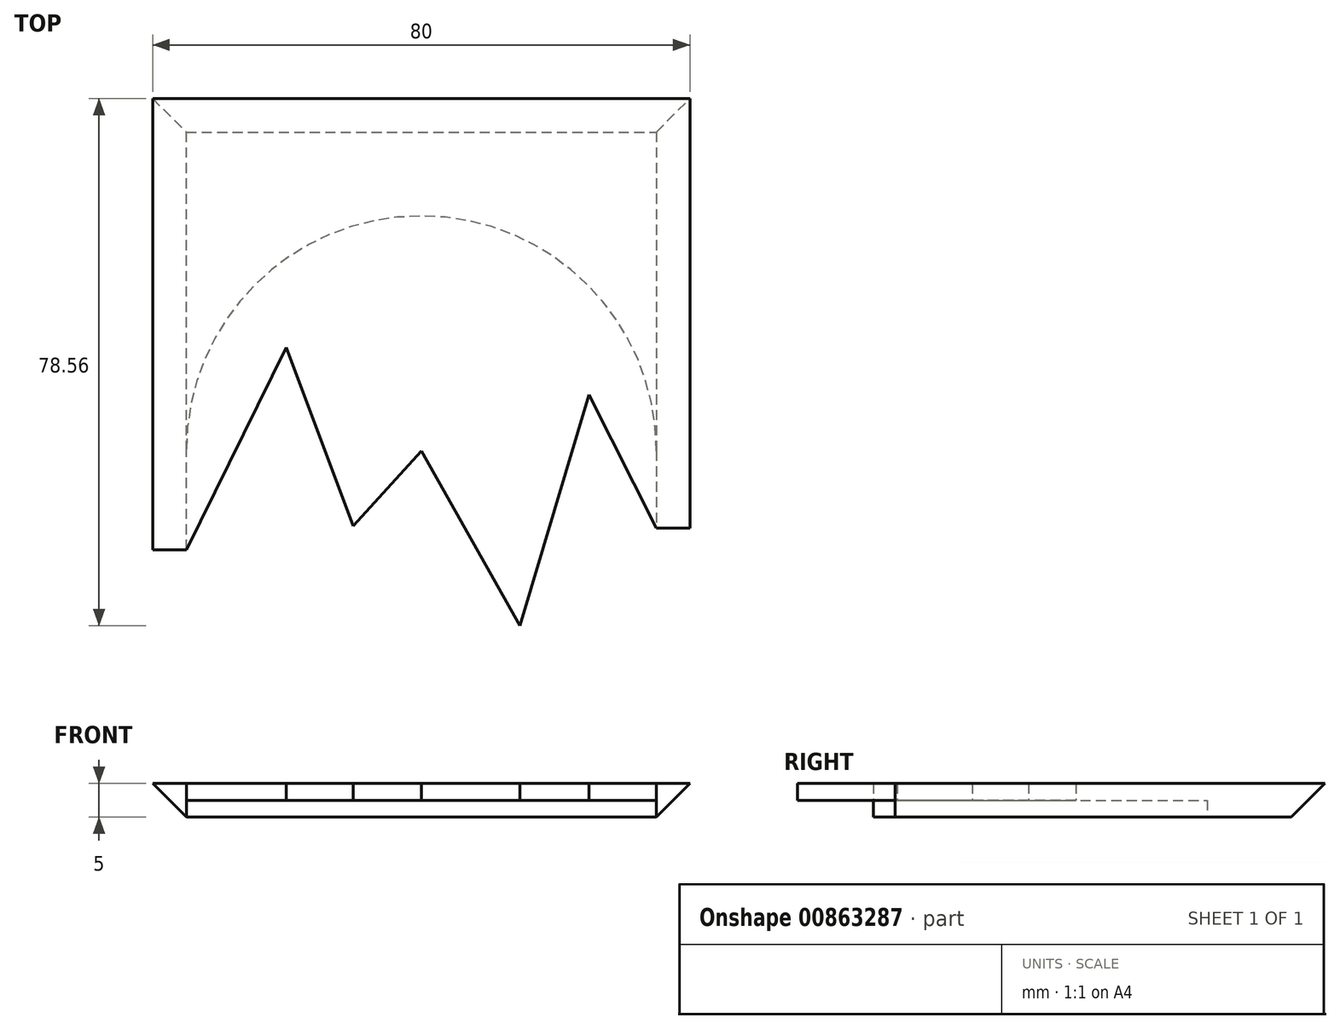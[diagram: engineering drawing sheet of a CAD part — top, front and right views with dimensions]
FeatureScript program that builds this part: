
annotation { "Feature Type Name" : "Feature", "Feature Type Description" : "" }
export const myFeature = defineFeature(function(context is Context, id is Id, definition is map)
    precondition{}
    {
        {
            var Q0;
            Q0=qCreatedBy(makeId("Top.planeOp"),FACE);
            var sketch = newSketch(context, id + "F0", { "sketchPlane" : qUnion([Q0])});
            skLineSegment(sketch, "E0.bottom", {"start": v(35, -47.5) * mm, "end": v(-35, -47.5) * mm});
            skLineSegment(sketch, "E0.top", {"start": v(35, 47.5) * mm, "end": v(-35, 47.5) * mm});
            skLineSegment(sketch, "E0.left", {"start": v(35, -47.5) * mm, "end": v(35, 47.5) * mm});
            skLineSegment(sketch, "E0.right", {"start": v(-35, -47.5) * mm, "end": v(-35, 47.5) * mm});
            skLineSegment(sketch, "E1.bottom", {"start": v(40, -52.5) * mm, "end": v(-40, -52.5) * mm});
            skLineSegment(sketch, "E1.top", {"start": v(40, 52.5) * mm, "end": v(-40, 52.5) * mm});
            skLineSegment(sketch, "E1.left", {"start": v(40, -52.5) * mm, "end": v(40, 52.5) * mm});
            skLineSegment(sketch, "E1.right", {"start": v(-40, -52.5) * mm, "end": v(-40, 52.5) * mm});
            skLineSegment(sketch, "E2", {"start": v(-35, -14.74) * mm, "end": v(-20.1, 15.44) * mm});
            skLineSegment(sketch, "E3", {"start": v(-20.1, 15.44) * mm, "end": v(-10.15, -11.19) * mm});
            skLineSegment(sketch, "E4", {"start": v(-10.15, -11.19) * mm, "end": v(0, 0) * mm});
            skLineSegment(sketch, "E5", {"start": v(0, 0) * mm, "end": v(14.7, -26.06) * mm});
            skLineSegment(sketch, "E6", {"start": v(14.7, -26.06) * mm, "end": v(25, 8.38) * mm});
            skLineSegment(sketch, "E7", {"start": v(25, 8.38) * mm, "end": v(35, -11.5) * mm});
            skLineSegment(sketch, "E8", {"start": v(35, -11.5) * mm, "end": v(40, -11.5) * mm});
            skLineSegment(sketch, "E9", {"start": v(-35, -14.74) * mm, "end": v(-40, -14.74) * mm});
            skSolve(sketch);
        }
        {
            var Q0;
            {var subQ1=sQuery(id+"F0.wireOp",EDGE,"E0.top");Q0=makeQuery(id+"F0.imprint","IMPRINT",FACE,{"disambiguationData":[TD([[makeQuery(id+"F0.imprint","IMPRINT",EDGE,{"derivedFrom":subQ1}),1.0]])]});}
            var Q1;
            {var subQ3=sQuery(id+"F0.wireOp",EDGE,"E0.top");Q1=makeQuery(id+"F0.imprint","IMPRINT",FACE,{"disambiguationData":[TD([[makeQuery(id+"F0.imprint","IMPRINT",EDGE,{"derivedFrom":subQ3}),-1.0]])]});}
            extrude(context, id + "F1", {"entities" : qUnion([Q0, Q1]), "depth" : 5 * mm, "offsetDistance" : 25 * mm});
        }
        {
            var Q0;
            Q0=makeQuery(id+"F1.opExtrude","CAP_EDGE",EDGE,{"disambiguationData":[OSD([sQuery(id+"F0.wireOp",EDGE,"E1.left")])],"isStart":true});
            var Q1;
            Q1=makeQuery(id+"F1.opExtrude","CAP_EDGE",EDGE,{"disambiguationData":[OSD([sQuery(id+"F0.wireOp",EDGE,"E1.top")])],"isStart":true});
            var Q2;
            Q2=makeQuery(id+"F1.opExtrude","CAP_EDGE",EDGE,{"disambiguationData":[OSD([sQuery(id+"F0.wireOp",EDGE,"E1.right")])],"isStart":true});
            chamfer(context, id + "F2", {"entities" : qUnion([Q0, Q1, Q2]), "width" : 5 * mm, "tangentPropagation" : true});
        }
        {
            var Q0;
            Q0=makeQuery(id+"F1.opExtrude","CAP_FACE",FACE,{"disambiguationData":[OSD([sQuery(id+"F0.wireOp",EDGE,"E1.top"),sQuery(id+"F0.wireOp",EDGE,"E1.left"),sQuery(id+"F0.wireOp",EDGE,"E1.right"),sQuery(id+"F0.wireOp",EDGE,"E2"),sQuery(id+"F0.wireOp",EDGE,"E3"),sQuery(id+"F0.wireOp",EDGE,"E4"),sQuery(id+"F0.wireOp",EDGE,"E5"),sQuery(id+"F0.wireOp",EDGE,"E6"),sQuery(id+"F0.wireOp",EDGE,"E7"),sQuery(id+"F0.wireOp",EDGE,"E8"),sQuery(id+"F0.wireOp",EDGE,"E9")])],"isStart":true});
            var sketch = newSketch(context, id + "F3", { "sketchPlane" : qUnion([Q0])});
            skCircle(sketch, "E10", {"center": v(0, 0) * mm, "radius": 35 * mm});
            skLineSegment(sketch, "E11", {"start": v(35, 0) * mm, "end": v(35, 26.42) * mm});
            skLineSegment(sketch, "E12", {"start": v(35, 26.42) * mm, "end": v(-35, 26.06) * mm});
            skLineSegment(sketch, "E13", {"start": v(-35, 26.06) * mm, "end": v(-35, 0) * mm});
            skSolve(sketch);
        }
        {
            var Q0;
            {var subQ0=sQuery(id+"F3.wireOp",EDGE,"E11");var subQ2=sQuery(id+"F0.wireOp",EDGE,"E7");var subQ5=makeQuery(id+"F1.opExtrude","CAP_EDGE",EDGE,{"disambiguationData":[OSD([subQ2])],"isStart":true});var subQ7=makeQuery(id+"F3.imprint","INTERSECT",VERTEX,{"derivedFrom":[subQ5,subQ0]});Q0=makeQuery(id+"F3.imprint","IMPRINT",FACE,{"disambiguationData":[TD([[makeQuery(id+"F3.imprint","IMPRINT",EDGE,{"disambiguationData":[TD([[subQ7,1.0]])],"derivedFrom":subQ5}),-1.0]])]});}
            var Q1;
            {var subQ0=sQuery(id+"F3.wireOp",EDGE,"E13");var subQ2=sQuery(id+"F0.wireOp",EDGE,"E2");var subQ5=makeQuery(id+"F1.opExtrude","CAP_EDGE",EDGE,{"disambiguationData":[OSD([subQ2])],"isStart":true});var subQ7=makeQuery(id+"F3.imprint","INTERSECT",VERTEX,{"derivedFrom":[subQ5,subQ0]});Q1=makeQuery(id+"F3.imprint","IMPRINT",FACE,{"disambiguationData":[TD([[makeQuery(id+"F3.imprint","IMPRINT",EDGE,{"disambiguationData":[TD([[subQ7,-1.0]])],"derivedFrom":subQ5}),-1.0]])]});}
            var Q2;
            {var subQ0=sQuery(id+"F0.wireOp",EDGE,"E3");var subQ1=makeQuery(id+"F1.opExtrude","CAP_EDGE",EDGE,{"disambiguationData":[OSD([subQ0])],"isStart":true});Q2=makeQuery(id+"F3.imprint","IMPRINT",FACE,{"disambiguationData":[TD([[makeQuery(id+"F3.imprint","IMPRINT",EDGE,{"derivedFrom":subQ1}),-1.0]])]});}
            extrude(context, id + "F4", {"entities" : qUnion([Q0, Q1, Q2]), "operationType" : NewBodyOperationType.REMOVE, "oppositeDirection" : true, "depth" : 2.5 * mm, "offsetDistance" : 25 * mm});
        }
    });
